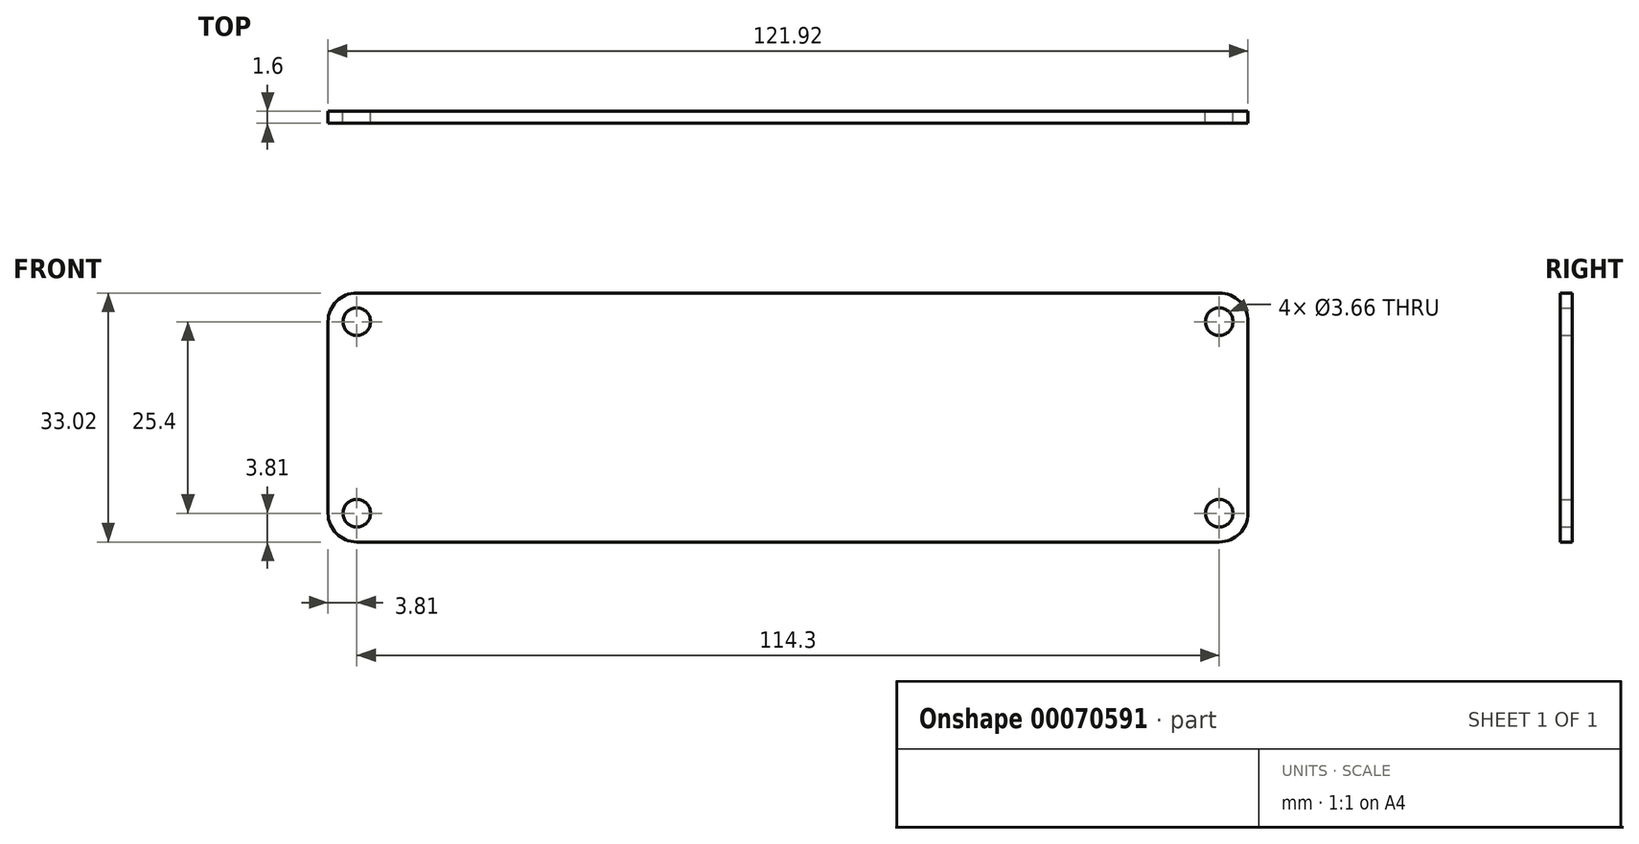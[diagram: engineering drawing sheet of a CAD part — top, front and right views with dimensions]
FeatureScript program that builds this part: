
annotation { "Feature Type Name" : "Feature", "Feature Type Description" : "" }
export const myFeature = defineFeature(function(context is Context, id is Id, definition is map)
    precondition{}
    {
        {
            var Q0;
            Q0=qCreatedBy(makeId("Front.planeOp"),FACE);
            var sketch = newSketch(context, id + "F0", { "sketchPlane" : qUnion([Q0])});
            skLineSegment(sketch, "E0.bottom", {"start": v(57.15, 16.51) * mm, "end": v(-57.15, 16.51) * mm});
            skLineSegment(sketch, "E0.top", {"start": v(57.15, -16.51) * mm, "end": v(-57.15, -16.51) * mm});
            skLineSegment(sketch, "E0.left", {"start": v(60.96, 12.7) * mm, "end": v(60.96, -12.7) * mm});
            skLineSegment(sketch, "E0.right", {"start": v(-60.96, 12.7) * mm, "end": v(-60.96, -12.7) * mm});
            skPoint(sketch, "E0.middle", {"position": v(0, 0) * mm});
            skCircle(sketch, "E1", {"center": v(-57.15, 12.7) * mm, "radius": 1.83 * mm});
            skCircle(sketch, "E2", {"center": v(-57.15, -12.7) * mm, "radius": 1.83 * mm});
            skCircle(sketch, "E3", {"center": v(57.15, 12.7) * mm, "radius": 1.83 * mm});
            skCircle(sketch, "E4", {"center": v(57.15, -12.7) * mm, "radius": 1.83 * mm});
            skLineSegment(sketch, "E5", {"start": v(-57.15, 12.7) * mm, "end": v(57.15, -12.7) * mm, "construction": true});
            skPoint(sketch, "E6.visualSharp", {"position": v(-60.96, 16.51) * mm});
            skArc(sketch, "E6.filletArc", {"start": v(-57.15, 16.51) * mm, "mid": v(-59.84, 15.4) * mm, "end": v(-60.96, 12.7) * mm});
            skPoint(sketch, "E7.visualSharp", {"position": v(-60.96, -16.51) * mm});
            skArc(sketch, "E7.filletArc", {"start": v(-60.96, -12.7) * mm, "mid": v(-59.84, -15.4) * mm, "end": v(-57.15, -16.51) * mm});
            skPoint(sketch, "E8.visualSharp", {"position": v(60.96, -16.51) * mm});
            skArc(sketch, "E8.filletArc", {"start": v(57.15, -16.51) * mm, "mid": v(59.84, -15.4) * mm, "end": v(60.96, -12.7) * mm});
            skPoint(sketch, "E9.visualSharp", {"position": v(60.96, 16.51) * mm});
            skArc(sketch, "E9.filletArc", {"start": v(60.96, 12.7) * mm, "mid": v(59.84, 15.4) * mm, "end": v(57.15, 16.51) * mm});
            skSolve(sketch);
        }
        {
            var Q0;
            Q0=makeQuery(id+"F0.imprint","IMPRINT",FACE,{"disambiguationData":[TD([[makeQuery(id+"F0.imprint","IMPRINT",EDGE,{"derivedFrom":sQuery(id+"F0.wireOp",EDGE,"E0.bottom")}),1.0]])]});
            extrude(context, id + "F1", {"entities" : qUnion([Q0]), "depth" : 1.6 * mm});
        }
    });
